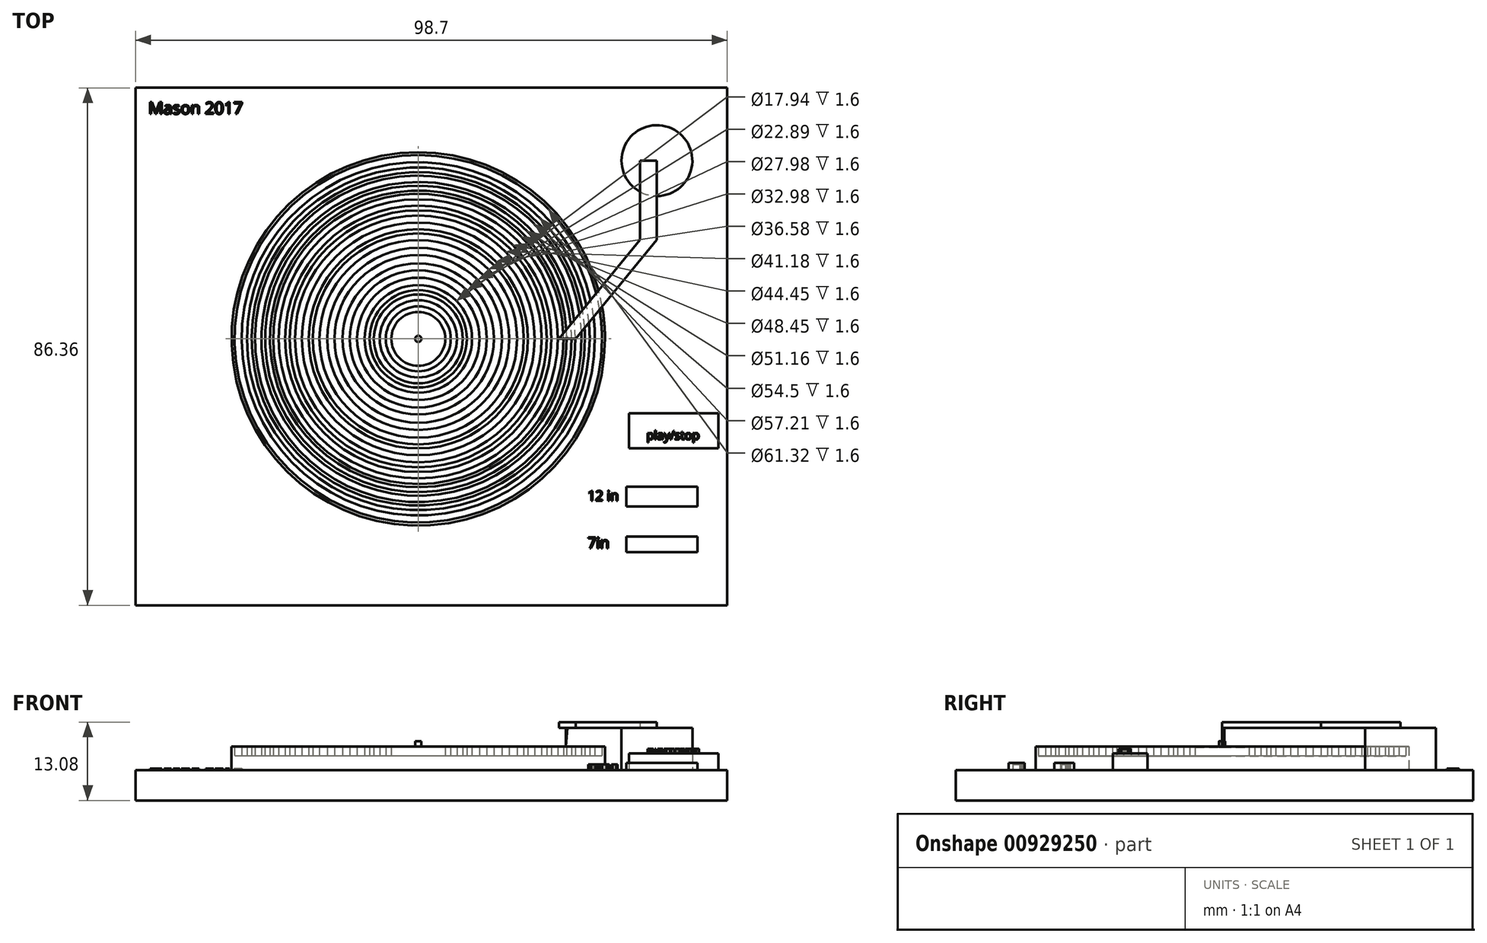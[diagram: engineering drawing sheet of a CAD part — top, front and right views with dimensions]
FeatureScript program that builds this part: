
annotation { "Feature Type Name" : "Feature", "Feature Type Description" : "" }
export const myFeature = defineFeature(function(context is Context, id is Id, definition is map)
    precondition{}
    {
        {
            var Q0;
            Q0=qCreatedBy(makeId("Top.planeOp"),FACE);
            var sketch = newSketch(context, id + "F0", { "sketchPlane" : qUnion([Q0])});
            skLineSegment(sketch, "E0.bottom", {"start": v(-47.16, 41.9) * mm, "end": v(51.54, 41.9) * mm});
            skLineSegment(sketch, "E0.top", {"start": v(-47.16, -44.46) * mm, "end": v(51.54, -44.46) * mm});
            skLineSegment(sketch, "E0.left", {"start": v(-47.16, 41.9) * mm, "end": v(-47.16, -44.46) * mm});
            skLineSegment(sketch, "E0.right", {"start": v(51.54, 41.9) * mm, "end": v(51.54, -44.46) * mm});
            skSolve(sketch);
        }
        {
            var Q0;
            Q0=qSketchRegion(id+"F0",true);
            extrude(context, id + "F1", {"entities" : qUnion([Q0]), "depth" : 5.08 * mm, "offsetDistance" : 25.4 * mm});
        }
        {
            var Q0;
            Q0=makeQuery(id+"F1.opExtrude","CAP_FACE",FACE,{"disambiguationData":[OSD([sQuery(id+"F0.wireOp",EDGE,"E0.bottom"),sQuery(id+"F0.wireOp",EDGE,"E0.top"),sQuery(id+"F0.wireOp",EDGE,"E0.left"),sQuery(id+"F0.wireOp",EDGE,"E0.right")])],"isStart":false});
            var sketch = newSketch(context, id + "F2", { "sketchPlane" : qUnion([Q0])});
            skCircle(sketch, "E1", {"center": v(0, 0) * mm, "radius": 31.16 * mm});
            skSolve(sketch);
        }
        {
            var Q0;
            Q0=qSketchRegion(id+"F2",true);
            extrude(context, id + "F3", {"entities" : qUnion([Q0]), "operationType" : NewBodyOperationType.ADD, "depth" : 2.3 * mm, "offsetDistance" : 25 * mm});
        }
        {
            var Q0;
            Q0=makeQuery(id+"F3.opExtrude","CAP_FACE",FACE,{"disambiguationData":[OSD([sQuery(id+"F2.wireOp",EDGE,"E1")])],"isStart":false});
            var sketch = newSketch(context, id + "F4", { "sketchPlane" : qUnion([Q0])});
            skCircle(sketch, "E2", {"center": v(0, 0) * mm, "radius": 5.42 * mm});
            skCircle(sketch, "E3", {"center": v(0, 0) * mm, "radius": 6.45 * mm});
            skCircle(sketch, "E4", {"center": v(0, 0) * mm, "radius": 7.42 * mm});
            skCircle(sketch, "E5", {"center": v(0, 0) * mm, "radius": 8.12 * mm});
            skCircle(sketch, "E6", {"center": v(0, 0) * mm, "radius": 8.97 * mm});
            skCircle(sketch, "E7", {"center": v(0, 0) * mm, "radius": 10.21 * mm});
            skCircle(sketch, "E8", {"center": v(0, 0) * mm, "radius": 11.44 * mm});
            skCircle(sketch, "E9", {"center": v(0, 0) * mm, "radius": 12.63 * mm});
            skCircle(sketch, "E10", {"center": v(0, 0) * mm, "radius": 14 * mm});
            skCircle(sketch, "E11", {"center": v(0, 0) * mm, "radius": 15.19 * mm});
            skCircle(sketch, "E12", {"center": v(0, 0) * mm, "radius": 16.49 * mm});
            skCircle(sketch, "E13", {"center": v(0, 0) * mm, "radius": 18.3 * mm});
            skCircle(sketch, "E14", {"center": v(0, 0) * mm, "radius": 19.42 * mm});
            skCircle(sketch, "E15", {"center": v(0, 0) * mm, "radius": 17.6 * mm});
            skCircle(sketch, "E16", {"center": v(0, 0) * mm, "radius": 20.59 * mm});
            skCircle(sketch, "E17", {"center": v(0, 0) * mm, "radius": 21.45 * mm});
            skCircle(sketch, "E18", {"center": v(0, 0) * mm, "radius": 23.3 * mm});
            skCircle(sketch, "E19", {"center": v(0, 0) * mm, "radius": 24.76 * mm});
            skCircle(sketch, "E20", {"center": v(0, 0) * mm, "radius": 22.23 * mm});
            skCircle(sketch, "E21", {"center": v(0, 0) * mm, "radius": 24.23 * mm});
            skCircle(sketch, "E22", {"center": v(0, 0) * mm, "radius": 26.2 * mm});
            skCircle(sketch, "E23", {"center": v(0, 0) * mm, "radius": 25.58 * mm});
            skCircle(sketch, "E24", {"center": v(0, 0) * mm, "radius": 27.81 * mm});
            skCircle(sketch, "E25", {"center": v(0, 0) * mm, "radius": 27.25 * mm});
            skCircle(sketch, "E26", {"center": v(0, 0) * mm, "radius": 29.49 * mm});
            skCircle(sketch, "E27", {"center": v(0, 0) * mm, "radius": 30.66 * mm});
            skCircle(sketch, "E28", {"center": v(0, 0) * mm, "radius": 28.6 * mm});
            skSolve(sketch);
        }
        {
            var Q0;
            Q0=makeQuery(id+"F4.imprint","IMPRINT",FACE,{"disambiguationData":[TD([[makeQuery(id+"F4.imprint","IMPRINT",EDGE,{"derivedFrom":sQuery(id+"F4.wireOp",EDGE,"E2")}),-1.0]])]});
            var Q1;
            Q1=makeQuery(id+"F4.imprint","IMPRINT",FACE,{"disambiguationData":[TD([[makeQuery(id+"F4.imprint","IMPRINT",EDGE,{"derivedFrom":sQuery(id+"F4.wireOp",EDGE,"E4")}),-1.0]])]});
            var Q2;
            Q2=makeQuery(id+"F4.imprint","IMPRINT",FACE,{"disambiguationData":[TD([[makeQuery(id+"F4.imprint","IMPRINT",EDGE,{"derivedFrom":sQuery(id+"F4.wireOp",EDGE,"E6")}),-1.0]])]});
            var Q3;
            Q3=makeQuery(id+"F4.imprint","IMPRINT",FACE,{"disambiguationData":[TD([[makeQuery(id+"F4.imprint","IMPRINT",EDGE,{"derivedFrom":sQuery(id+"F4.wireOp",EDGE,"E8")}),-1.0]])]});
            var Q4;
            Q4=makeQuery(id+"F4.imprint","IMPRINT",FACE,{"disambiguationData":[TD([[makeQuery(id+"F4.imprint","IMPRINT",EDGE,{"derivedFrom":sQuery(id+"F4.wireOp",EDGE,"E10")}),-1.0]])]});
            var Q5;
            Q5=makeQuery(id+"F4.imprint","IMPRINT",FACE,{"disambiguationData":[TD([[makeQuery(id+"F4.imprint","IMPRINT",EDGE,{"derivedFrom":sQuery(id+"F4.wireOp",EDGE,"E12")}),-1.0]])]});
            var Q6;
            Q6=makeQuery(id+"F4.imprint","IMPRINT",FACE,{"disambiguationData":[TD([[makeQuery(id+"F4.imprint","IMPRINT",EDGE,{"derivedFrom":sQuery(id+"F4.wireOp",EDGE,"E13")}),-1.0]])]});
            var Q7;
            Q7=makeQuery(id+"F4.imprint","IMPRINT",FACE,{"disambiguationData":[TD([[makeQuery(id+"F4.imprint","IMPRINT",EDGE,{"derivedFrom":sQuery(id+"F4.wireOp",EDGE,"E16")}),-1.0]])]});
            var Q8;
            Q8=makeQuery(id+"F4.imprint","IMPRINT",FACE,{"disambiguationData":[TD([[makeQuery(id+"F4.imprint","IMPRINT",EDGE,{"derivedFrom":sQuery(id+"F4.wireOp",EDGE,"E18")}),1.0]])]});
            var Q9;
            Q9=makeQuery(id+"F4.imprint","IMPRINT",FACE,{"disambiguationData":[TD([[makeQuery(id+"F4.imprint","IMPRINT",EDGE,{"derivedFrom":sQuery(id+"F4.wireOp",EDGE,"E19")}),1.0]])]});
            var Q10;
            Q10=makeQuery(id+"F4.imprint","IMPRINT",FACE,{"disambiguationData":[TD([[makeQuery(id+"F4.imprint","IMPRINT",EDGE,{"derivedFrom":sQuery(id+"F4.wireOp",EDGE,"E22")}),1.0]])]});
            var Q11;
            Q11=makeQuery(id+"F4.imprint","IMPRINT",FACE,{"disambiguationData":[TD([[makeQuery(id+"F4.imprint","IMPRINT",EDGE,{"derivedFrom":sQuery(id+"F4.wireOp",EDGE,"E24")}),1.0]])]});
            var Q12;
            Q12=makeQuery(id+"F4.imprint","IMPRINT",FACE,{"disambiguationData":[TD([[makeQuery(id+"F4.imprint","IMPRINT",EDGE,{"derivedFrom":sQuery(id+"F4.wireOp",EDGE,"E26")}),1.0]])]});
            var Q13;
            Q13=makeQuery(id+"F4.imprint","IMPRINT",FACE,{"disambiguationData":[TD([[makeQuery(id+"F4.imprint","IMPRINT",EDGE,{"derivedFrom":sQuery(id+"F4.wireOp",EDGE,"E27")}),-1.0]])]});
            extrude(context, id + "F5", {"entities" : qUnion([Q0, Q1, Q2, Q3, Q4, Q5, Q6, Q7, Q8, Q9, Q10, Q11, Q12, Q13]), "operationType" : NewBodyOperationType.ADD, "depth" : 1.6 * mm, "offsetDistance" : 25 * mm});
        }
        {
            var Q0;
            Q0=makeQuery(id+"F1.opExtrude","CAP_FACE",FACE,{"disambiguationData":[OSD([sQuery(id+"F0.wireOp",EDGE,"E0.bottom"),sQuery(id+"F0.wireOp",EDGE,"E0.top"),sQuery(id+"F0.wireOp",EDGE,"E0.left"),sQuery(id+"F0.wireOp",EDGE,"E0.right")])],"isStart":false});
            var sketch = newSketch(context, id + "F6", { "sketchPlane" : qUnion([Q0])});
            skCircle(sketch, "E29", {"center": v(39.84, 29.75) * mm, "radius": 5.91 * mm});
            skSolve(sketch);
        }
        {
            var Q0;
            Q0=qSketchRegion(id+"F6",true);
            extrude(context, id + "F7", {"entities" : qUnion([Q0]), "operationType" : NewBodyOperationType.ADD, "depth" : 7 * mm, "offsetDistance" : 25 * mm});
        }
        {
            var Q0;
            Q0=makeQuery(id+"F7.opExtrude","CAP_FACE",FACE,{"disambiguationData":[OSD([sQuery(id+"F6.wireOp",EDGE,"E29")])],"isStart":false});
            var sketch = newSketch(context, id + "F8", { "sketchPlane" : qUnion([Q0])});
            skLineSegment(sketch, "E30", {"start": v(39.84, 29.75) * mm, "end": v(39.84, 16.51) * mm});
            skLineSegment(sketch, "E31", {"start": v(39.84, 16.51) * mm, "end": v(26.27, 0) * mm});
            skLineSegment(sketch, "E32", {"start": v(37.04, 29.75) * mm, "end": v(37.04, 16.51) * mm});
            skLineSegment(sketch, "E33", {"start": v(37.04, 16.51) * mm, "end": v(23.47, 0) * mm});
            skLineSegment(sketch, "E34", {"start": v(23.47, 0) * mm, "end": v(26.27, 0) * mm});
            skLineSegment(sketch, "E35", {"start": v(37.04, 29.75) * mm, "end": v(39.84, 29.75) * mm});
            skSolve(sketch);
        }
        {
            var Q0;
            {var subQ4=sQuery(id+"F8.wireOp",EDGE,"E31");Q0=makeQuery(id+"F8.imprint","IMPRINT",FACE,{"disambiguationData":[TD([[makeQuery(id+"F8.imprint","IMPRINT",EDGE,{"derivedFrom":subQ4}),-1.0]])]});}
            var Q1;
            {var subQ0=sQuery(id+"F8.wireOp",EDGE,"E35");Q1=makeQuery(id+"F8.imprint","IMPRINT",FACE,{"disambiguationData":[TD([[makeQuery(id+"F8.imprint","IMPRINT",EDGE,{"derivedFrom":subQ0}),-1.0]])]});}
            extrude(context, id + "F9", {"entities" : qUnion([Q0, Q1]), "operationType" : NewBodyOperationType.ADD, "depth" : 1 * mm, "offsetDistance" : 25 * mm});
        }
        {
            var Q0;
            Q0=makeQuery(id+"F9.opExtrude","SWEPT_FACE",FACE,{"disambiguationData":[OSD([sQuery(id+"F8.wireOp",EDGE,"E34")])]});
            var sketch = newSketch(context, id + "F10", { "sketchPlane" : qUnion([Q0])});
            skLineSegment(sketch, "E36", {"start": v(24.87, 12.08) * mm, "end": v(24.65, 8.95) * mm});
            skLineSegment(sketch, "E37", {"start": v(24.65, 8.95) * mm, "end": v(24.65, 12.08) * mm});
            skSolve(sketch);
        }
        {
            var Q0;
            {var subQ0=sQuery(id+"F10.wireOp",EDGE,"E36");Q0=makeQuery(id+"F10.imprint","IMPRINT",FACE,{"disambiguationData":[TD([[makeQuery(id+"F10.imprint","IMPRINT",EDGE,{"derivedFrom":subQ0}),-1.0]])]});}
            extrude(context, id + "F11", {"entities" : qUnion([Q0]), "oppositeDirection" : true, "depth" : 0.4 * mm, "offsetDistance" : 25 * mm});
        }
        {
            var Q0;
            Q0=makeQuery(id+"F5.boolean.opBoolean","SPLIT",FACE,{"disambiguationData":[TD([makeQuery(id+"F5.opExtrude","SWEPT_FACE",FACE,{"disambiguationData":[OSD([sQuery(id+"F4.wireOp",EDGE,"E2")])]})])],"derivedFrom":makeQuery(id+"F3.opExtrude","CAP_FACE",FACE,{"disambiguationData":[OSD([sQuery(id+"F2.wireOp",EDGE,"E1")])],"isStart":false})});
            var sketch = newSketch(context, id + "F12", { "sketchPlane" : qUnion([Q0])});
            skCircle(sketch, "E38", {"center": v(0, 0) * mm, "radius": 4.5 * mm});
            skSolve(sketch);
        }
        {
            var Q0;
            Q0=makeQuery(id+"F12.imprint","IMPRINT",FACE,{"disambiguationData":[TD([[makeQuery(id+"F12.imprint","IMPRINT",EDGE,{"derivedFrom":sQuery(id+"F12.wireOp",EDGE,"E38")}),1.0]])]});
            extrude(context, id + "F13", {"entities" : qUnion([Q0]), "operationType" : NewBodyOperationType.ADD, "depth" : 1.5 * mm, "offsetDistance" : 25 * mm});
        }
        {
            var Q0;
            Q0=makeQuery(id+"F13.opExtrude","CAP_FACE",FACE,{"disambiguationData":[OSD([sQuery(id+"F12.wireOp",EDGE,"E38")])],"isStart":false});
            var sketch = newSketch(context, id + "F14", { "sketchPlane" : qUnion([Q0])});
            skCircle(sketch, "E39", {"center": v(0, 0) * mm, "radius": 0.52 * mm});
            skSolve(sketch);
        }
        {
            var Q0;
            Q0=makeQuery(id+"F14.imprint","IMPRINT",FACE,{"disambiguationData":[TD([[makeQuery(id+"F14.imprint","IMPRINT",EDGE,{"derivedFrom":sQuery(id+"F14.wireOp",EDGE,"E39")}),1.0]])]});
            extrude(context, id + "F15", {"entities" : qUnion([Q0]), "operationType" : NewBodyOperationType.ADD, "depth" : 1 * mm, "offsetDistance" : 25 * mm});
        }
        {
            var Q0;
            Q0=makeQuery(id+"F1.opExtrude","CAP_FACE",FACE,{"disambiguationData":[OSD([sQuery(id+"F0.wireOp",EDGE,"E0.bottom"),sQuery(id+"F0.wireOp",EDGE,"E0.top"),sQuery(id+"F0.wireOp",EDGE,"E0.left"),sQuery(id+"F0.wireOp",EDGE,"E0.right")])],"isStart":false});
            var sketch = newSketch(context, id + "F16", { "sketchPlane" : qUnion([Q0])});
            skLineSegment(sketch, "E40.bottom", {"start": v(34.7, -24.7) * mm, "end": v(46.62, -24.7) * mm});
            skLineSegment(sketch, "E40.top", {"start": v(34.7, -28) * mm, "end": v(46.62, -28) * mm});
            skLineSegment(sketch, "E40.left", {"start": v(34.7, -24.7) * mm, "end": v(34.7, -28) * mm});
            skLineSegment(sketch, "E40.right", {"start": v(46.62, -24.7) * mm, "end": v(46.62, -28) * mm});
            skLineSegment(sketch, "E41.bottom", {"start": v(34.7, -32.97) * mm, "end": v(46.62, -32.97) * mm});
            skLineSegment(sketch, "E41.top", {"start": v(34.7, -35.61) * mm, "end": v(46.62, -35.61) * mm});
            skLineSegment(sketch, "E41.left", {"start": v(34.7, -32.97) * mm, "end": v(34.7, -35.61) * mm});
            skLineSegment(sketch, "E41.right", {"start": v(46.62, -32.97) * mm, "end": v(46.62, -35.61) * mm});
            skSolve(sketch);
        }
        {
            var Q0;
            Q0=qSketchRegion(id+"F16",true);
            extrude(context, id + "F17", {"entities" : qUnion([Q0]), "operationType" : NewBodyOperationType.ADD, "depth" : 1.2 * mm, "offsetDistance" : 25 * mm});
        }
        {
            var Q0;
            Q0=makeQuery(id+"F1.opExtrude","CAP_FACE",FACE,{"disambiguationData":[OSD([sQuery(id+"F0.wireOp",EDGE,"E0.bottom"),sQuery(id+"F0.wireOp",EDGE,"E0.top"),sQuery(id+"F0.wireOp",EDGE,"E0.left"),sQuery(id+"F0.wireOp",EDGE,"E0.right")])],"isStart":false});
            var sketch = newSketch(context, id + "F18", { "sketchPlane" : qUnion([Q0])});
            skText(sketch, "E42", { "text": "12 in", "fontName": "OpenSans-Regular.ttf"});
            skText(sketch, "E43", { "text": "7in", "fontName": "OpenSans-Regular.ttf"});
            const initialGuessF18  = {"E42": [0.02825, -0.027, 1, 0, 0.00165], "E43": [0.02825, -0.03495, 1, 0, 0.00182]};
            skSetInitialGuess(sketch, initialGuessF18);
            skSolve(sketch);
        }
        {
            var Q0;
            Q0=makeQuery(id+"F18.imprint","IMPRINT",FACE,{"disambiguationData":[TD([[makeQuery(id+"F18.imprint","IMPRINT",EDGE,{"derivedFrom":sQuery(id+"F18.wireOp",EDGE,"E43.sketch_text.stroke-0")}),-1.0]])]});
            var Q1;
            Q1=makeQuery(id+"F18.imprint","IMPRINT",FACE,{"disambiguationData":[TD([[makeQuery(id+"F18.imprint","IMPRINT",EDGE,{"derivedFrom":sQuery(id+"F18.wireOp",EDGE,"E43.sketch_text.stroke-7")}),-1.0]])]});
            var Q2;
            Q2=makeQuery(id+"F18.imprint","IMPRINT",FACE,{"disambiguationData":[TD([[makeQuery(id+"F18.imprint","IMPRINT",EDGE,{"derivedFrom":sQuery(id+"F18.wireOp",EDGE,"E43.sketch_text.stroke-11")}),-1.0]])]});
            var Q3;
            Q3=makeQuery(id+"F18.imprint","IMPRINT",FACE,{"disambiguationData":[TD([[makeQuery(id+"F18.imprint","IMPRINT",EDGE,{"derivedFrom":sQuery(id+"F18.wireOp",EDGE,"E43.sketch_text.stroke-19")}),-1.0]])]});
            var Q4;
            Q4=makeQuery(id+"F18.imprint","IMPRINT",FACE,{"disambiguationData":[TD([[makeQuery(id+"F18.imprint","IMPRINT",EDGE,{"derivedFrom":sQuery(id+"F18.wireOp",EDGE,"E42.sketch_text.stroke-9")}),-1.0]])]});
            var Q5;
            Q5=makeQuery(id+"F18.imprint","IMPRINT",FACE,{"disambiguationData":[TD([[makeQuery(id+"F18.imprint","IMPRINT",EDGE,{"derivedFrom":sQuery(id+"F18.wireOp",EDGE,"E42.sketch_text.stroke-0")}),-1.0]])]});
            var Q6;
            Q6=makeQuery(id+"F18.imprint","IMPRINT",FACE,{"disambiguationData":[TD([[makeQuery(id+"F18.imprint","IMPRINT",EDGE,{"derivedFrom":sQuery(id+"F18.wireOp",EDGE,"E42.sketch_text.stroke-29")}),-1.0]])]});
            var Q7;
            Q7=makeQuery(id+"F18.imprint","IMPRINT",FACE,{"disambiguationData":[TD([[makeQuery(id+"F18.imprint","IMPRINT",EDGE,{"derivedFrom":sQuery(id+"F18.wireOp",EDGE,"E42.sketch_text.stroke-33")}),-1.0]])]});
            var Q8;
            Q8=makeQuery(id+"F18.imprint","IMPRINT",FACE,{"disambiguationData":[TD([[makeQuery(id+"F18.imprint","IMPRINT",EDGE,{"derivedFrom":sQuery(id+"F18.wireOp",EDGE,"E42.sketch_text.stroke-41")}),-1.0]])]});
            extrude(context, id + "F19", {"entities" : qUnion([Q0, Q1, Q2, Q3, Q4, Q5, Q6, Q7, Q8]), "operationType" : NewBodyOperationType.ADD, "depth" : 0.9 * mm, "offsetDistance" : 25 * mm});
        }
        {
            var Q0;
            Q0=makeQuery(id+"F1.opExtrude","CAP_FACE",FACE,{"disambiguationData":[OSD([sQuery(id+"F0.wireOp",EDGE,"E0.bottom"),sQuery(id+"F0.wireOp",EDGE,"E0.top"),sQuery(id+"F0.wireOp",EDGE,"E0.left"),sQuery(id+"F0.wireOp",EDGE,"E0.right")])],"isStart":false});
            var sketch = newSketch(context, id + "F20", { "sketchPlane" : qUnion([Q0])});
            skLineSegment(sketch, "E44.bottom", {"start": v(35.2, -12.45) * mm, "end": v(50.1, -12.45) * mm});
            skLineSegment(sketch, "E44.top", {"start": v(35.2, -18.24) * mm, "end": v(50.1, -18.24) * mm});
            skLineSegment(sketch, "E44.left", {"start": v(35.2, -12.45) * mm, "end": v(35.2, -18.24) * mm});
            skLineSegment(sketch, "E44.right", {"start": v(50.1, -12.45) * mm, "end": v(50.1, -18.24) * mm});
            skSolve(sketch);
        }
        {
            var Q0;
            Q0=makeQuery(id+"F20.imprint","IMPRINT",FACE,{"disambiguationData":[TD([[makeQuery(id+"F20.imprint","IMPRINT",EDGE,{"derivedFrom":sQuery(id+"F20.wireOp",EDGE,"E44.bottom")}),-1.0]])]});
            extrude(context, id + "F21", {"entities" : qUnion([Q0]), "operationType" : NewBodyOperationType.ADD, "depth" : 2.8 * mm, "offsetDistance" : 25 * mm});
        }
        {
            var Q0;
            Q0=makeQuery(id+"F21.opExtrude","CAP_FACE",FACE,{"disambiguationData":[OSD([sQuery(id+"F20.wireOp",EDGE,"E44.bottom"),sQuery(id+"F20.wireOp",EDGE,"E44.top"),sQuery(id+"F20.wireOp",EDGE,"E44.left"),sQuery(id+"F20.wireOp",EDGE,"E44.right")])],"isStart":false});
            var sketch = newSketch(context, id + "F22", { "sketchPlane" : qUnion([Q0])});
            skText(sketch, "E45", { "text": "play/stop", "fontName": "OpenSans-Regular.ttf"});
            skPoint(sketch, "E45.firstSnap0", {"position": v(35.2, -15.34) * mm});
            const initialGuessF22  = {"E45": [0.03808, -0.01681, 1, 0, 0.00147]};
            skSetInitialGuess(sketch, initialGuessF22);
            skSolve(sketch);
        }
        {
            var Q0;
            Q0=makeQuery(id+"F22.imprint","IMPRINT",FACE,{"disambiguationData":[TD([[makeQuery(id+"F22.imprint","IMPRINT",EDGE,{"derivedFrom":sQuery(id+"F22.wireOp",EDGE,"E45.sketch_text.stroke-0")}),-1.0]])]});
            var Q1;
            Q1=makeQuery(id+"F22.imprint","IMPRINT",FACE,{"disambiguationData":[TD([[makeQuery(id+"F22.imprint","IMPRINT",EDGE,{"derivedFrom":sQuery(id+"F22.wireOp",EDGE,"E45.sketch_text.stroke-25")}),-1.0]])]});
            var Q2;
            Q2=makeQuery(id+"F22.imprint","IMPRINT",FACE,{"disambiguationData":[TD([[makeQuery(id+"F22.imprint","IMPRINT",EDGE,{"derivedFrom":sQuery(id+"F22.wireOp",EDGE,"E45.sketch_text.stroke-29")}),-1.0]])]});
            var Q3;
            Q3=makeQuery(id+"F22.imprint","IMPRINT",FACE,{"disambiguationData":[TD([[makeQuery(id+"F22.imprint","IMPRINT",EDGE,{"derivedFrom":sQuery(id+"F22.wireOp",EDGE,"E45.sketch_text.stroke-56")}),-1.0]])]});
            var Q4;
            Q4=makeQuery(id+"F22.imprint","IMPRINT",FACE,{"disambiguationData":[TD([[makeQuery(id+"F22.imprint","IMPRINT",EDGE,{"derivedFrom":sQuery(id+"F22.wireOp",EDGE,"E45.sketch_text.stroke-72")}),-1.0]])]});
            var Q5;
            Q5=makeQuery(id+"F22.imprint","IMPRINT",FACE,{"disambiguationData":[TD([[makeQuery(id+"F22.imprint","IMPRINT",EDGE,{"derivedFrom":sQuery(id+"F22.wireOp",EDGE,"E45.sketch_text.stroke-76")}),-1.0]])]});
            var Q6;
            Q6=makeQuery(id+"F22.imprint","IMPRINT",FACE,{"disambiguationData":[TD([[makeQuery(id+"F22.imprint","IMPRINT",EDGE,{"derivedFrom":sQuery(id+"F22.wireOp",EDGE,"E45.sketch_text.stroke-101")}),-1.0]])]});
            var Q7;
            Q7=makeQuery(id+"F22.imprint","IMPRINT",FACE,{"disambiguationData":[TD([[makeQuery(id+"F22.imprint","IMPRINT",EDGE,{"derivedFrom":sQuery(id+"F22.wireOp",EDGE,"E45.sketch_text.stroke-120")}),-1.0]])]});
            var Q8;
            Q8=makeQuery(id+"F22.imprint","IMPRINT",FACE,{"disambiguationData":[TD([[makeQuery(id+"F22.imprint","IMPRINT",EDGE,{"derivedFrom":sQuery(id+"F22.wireOp",EDGE,"E45.sketch_text.stroke-137")}),-1.0]])]});
            extrude(context, id + "F23", {"entities" : qUnion([Q0, Q1, Q2, Q3, Q4, Q5, Q6, Q7, Q8]), "operationType" : NewBodyOperationType.ADD, "depth" : 0.7 * mm, "offsetDistance" : 25 * mm});
        }
        {
            var Q0;
            Q0=makeQuery(id+"F1.opExtrude","CAP_FACE",FACE,{"disambiguationData":[OSD([sQuery(id+"F0.wireOp",EDGE,"E0.bottom"),sQuery(id+"F0.wireOp",EDGE,"E0.top"),sQuery(id+"F0.wireOp",EDGE,"E0.left"),sQuery(id+"F0.wireOp",EDGE,"E0.right")])],"isStart":false});
            var sketch = newSketch(context, id + "F24", { "sketchPlane" : qUnion([Q0])});
            skText(sketch, "E46", { "text": "Mason 2017", "fontName": "OpenSans-Regular.ttf"});
            const initialGuessF24  = {"E46": [-0.04505, 0.03753, 1, 0, 0.00199]};
            skSetInitialGuess(sketch, initialGuessF24);
            skSolve(sketch);
        }
        {
            var Q0;
            Q0=makeQuery(id+"F24.imprint","IMPRINT",FACE,{"disambiguationData":[TD([[makeQuery(id+"F24.imprint","IMPRINT",EDGE,{"derivedFrom":sQuery(id+"F24.wireOp",EDGE,"E46.sketch_text.stroke-0")}),-1.0]])]});
            var Q1;
            Q1=makeQuery(id+"F24.imprint","IMPRINT",FACE,{"disambiguationData":[TD([[makeQuery(id+"F24.imprint","IMPRINT",EDGE,{"derivedFrom":sQuery(id+"F24.wireOp",EDGE,"E46.sketch_text.stroke-18")}),-1.0]])]});
            var Q2;
            Q2=makeQuery(id+"F24.imprint","IMPRINT",FACE,{"disambiguationData":[TD([[makeQuery(id+"F24.imprint","IMPRINT",EDGE,{"derivedFrom":sQuery(id+"F24.wireOp",EDGE,"E46.sketch_text.stroke-45")}),-1.0]])]});
            var Q3;
            Q3=makeQuery(id+"F24.imprint","IMPRINT",FACE,{"disambiguationData":[TD([[makeQuery(id+"F24.imprint","IMPRINT",EDGE,{"derivedFrom":sQuery(id+"F24.wireOp",EDGE,"E46.sketch_text.stroke-70")}),-1.0]])]});
            var Q4;
            Q4=makeQuery(id+"F24.imprint","IMPRINT",FACE,{"disambiguationData":[TD([[makeQuery(id+"F24.imprint","IMPRINT",EDGE,{"derivedFrom":sQuery(id+"F24.wireOp",EDGE,"E46.sketch_text.stroke-87")}),-1.0]])]});
            var Q5;
            Q5=makeQuery(id+"F24.imprint","IMPRINT",FACE,{"disambiguationData":[TD([[makeQuery(id+"F24.imprint","IMPRINT",EDGE,{"derivedFrom":sQuery(id+"F24.wireOp",EDGE,"E46.sketch_text.stroke-104")}),-1.0]])]});
            var Q6;
            Q6=makeQuery(id+"F24.imprint","IMPRINT",FACE,{"disambiguationData":[TD([[makeQuery(id+"F24.imprint","IMPRINT",EDGE,{"derivedFrom":sQuery(id+"F24.wireOp",EDGE,"E46.sketch_text.stroke-124")}),-1.0]])]});
            var Q7;
            Q7=makeQuery(id+"F24.imprint","IMPRINT",FACE,{"disambiguationData":[TD([[makeQuery(id+"F24.imprint","IMPRINT",EDGE,{"derivedFrom":sQuery(id+"F24.wireOp",EDGE,"E46.sketch_text.stroke-140")}),-1.0]])]});
            var Q8;
            Q8=makeQuery(id+"F24.imprint","IMPRINT",FACE,{"disambiguationData":[TD([[makeQuery(id+"F24.imprint","IMPRINT",EDGE,{"derivedFrom":sQuery(id+"F24.wireOp",EDGE,"E46.sketch_text.stroke-149")}),-1.0]])]});
            extrude(context, id + "F25", {"entities" : qUnion([Q0, Q1, Q2, Q3, Q4, Q5, Q6, Q7, Q8]), "operationType" : NewBodyOperationType.ADD, "depth" : 0.2 * mm, "offsetDistance" : 25 * mm});
        }
    });
